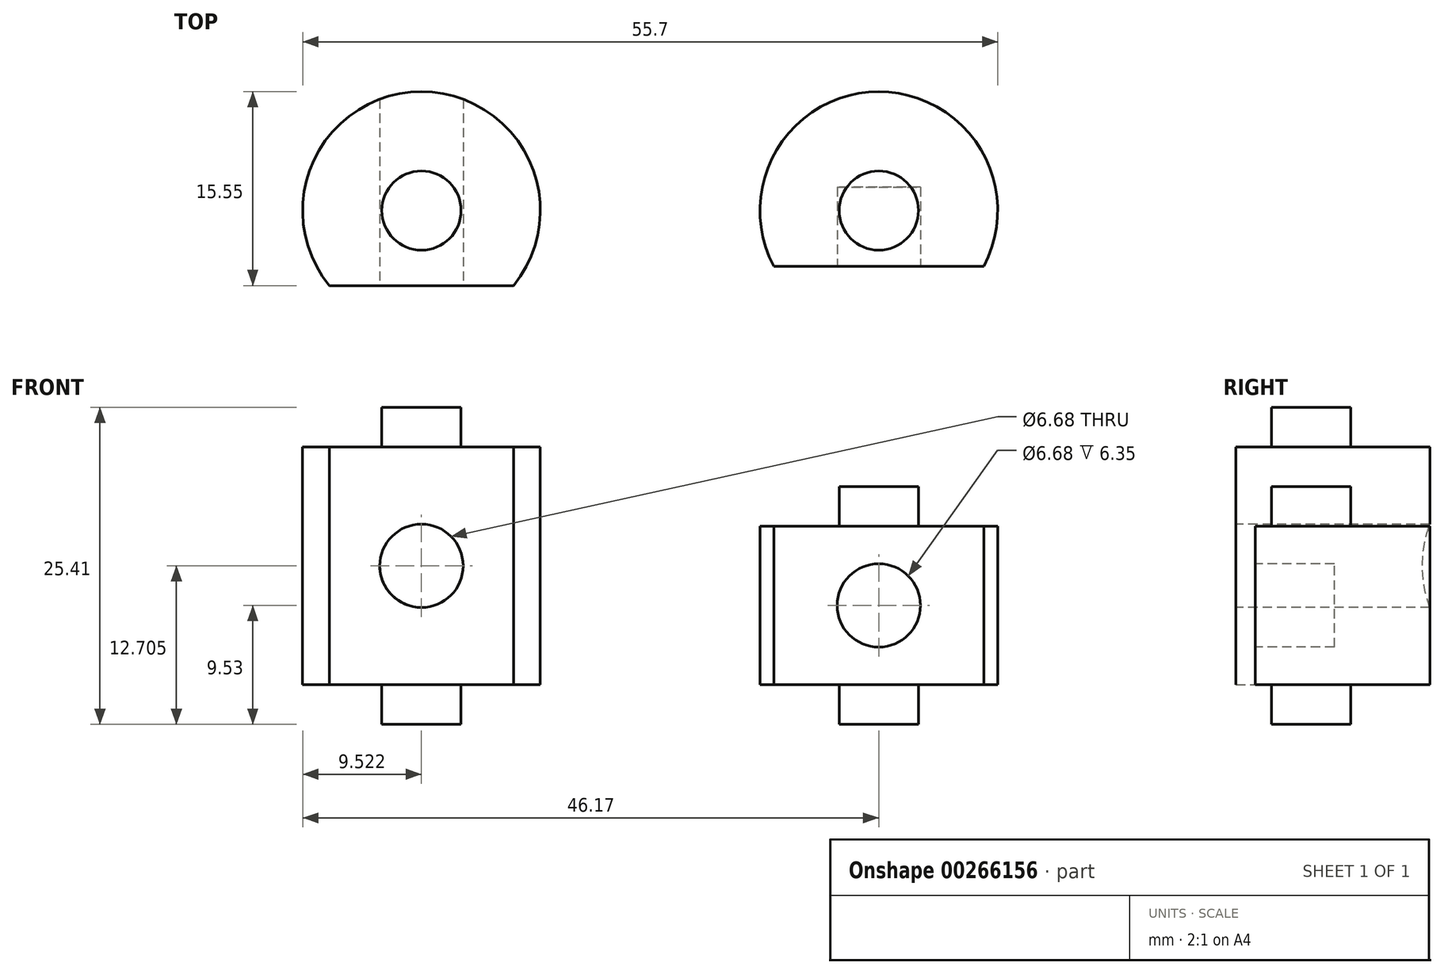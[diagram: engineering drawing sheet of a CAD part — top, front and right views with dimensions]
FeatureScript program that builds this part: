
annotation { "Feature Type Name" : "Feature", "Feature Type Description" : "" }
export const myFeature = defineFeature(function(context is Context, id is Id, definition is map)
    precondition{}
    {
        {
            var Q0;
            Q0=qCreatedBy(makeId("Top.planeOp"),FACE);
            var sketch = newSketch(context, id + "F0", { "sketchPlane" : qUnion([Q0])});
            skCircle(sketch, "E0", {"center": v(0, 0) * mm, "radius": 9.53 * mm});
            skSolve(sketch);
        }
        {
            var Q0;
            Q0=makeQuery(id+"F0.imprint","IMPRINT",FACE,{"disambiguationData":[TD([[makeQuery(id+"F0.imprint","IMPRINT",EDGE,{"derivedFrom":sQuery(id+"F0.wireOp",EDGE,"E0")}),1.0]])]});
            extrude(context, id + "F1", {"entities" : qUnion([Q0]), "depth" : 12.7 * mm});
        }
        {
            var Q0;
            Q0=makeQuery(id+"F1.opExtrude","CAP_FACE",FACE,{"disambiguationData":[OSD([sQuery(id+"F0.wireOp",EDGE,"E0")])],"isStart":false});
            var sketch = newSketch(context, id + "F2", { "sketchPlane" : qUnion([Q0])});
            skCircle(sketch, "E1", {"center": v(0, 0) * mm, "radius": 3.18 * mm});
            skSolve(sketch);
        }
        {
            var Q0;
            Q0=makeQuery(id+"F2.imprint","IMPRINT",FACE,{"disambiguationData":[TD([[makeQuery(id+"F2.imprint","IMPRINT",EDGE,{"derivedFrom":sQuery(id+"F2.wireOp",EDGE,"E1")}),1.0]])]});
            extrude(context, id + "F3", {"entities" : qUnion([Q0]), "operationType" : NewBodyOperationType.ADD, "depth" : 3.17 * mm});
        }
        {
            var Q0;
            Q0=makeQuery(id+"F1.opExtrude","CAP_FACE",FACE,{"disambiguationData":[OSD([sQuery(id+"F0.wireOp",EDGE,"E0")])],"isStart":true});
            var sketch = newSketch(context, id + "F4", { "sketchPlane" : qUnion([Q0])});
            skCircle(sketch, "E2", {"center": v(0, 0) * mm, "radius": 3.18 * mm});
            skSolve(sketch);
        }
        {
            var Q0;
            Q0=makeQuery(id+"F4.imprint","IMPRINT",FACE,{"disambiguationData":[TD([[makeQuery(id+"F4.imprint","IMPRINT",EDGE,{"derivedFrom":sQuery(id+"F4.wireOp",EDGE,"E2")}),1.0]])]});
            extrude(context, id + "F5", {"entities" : qUnion([Q0]), "operationType" : NewBodyOperationType.ADD, "depth" : 3.17 * mm});
        }
        {
            var Q0;
            Q0=qCreatedBy(makeId("Top.planeOp"),FACE);
            var sketch = newSketch(context, id + "F6", { "sketchPlane" : qUnion([Q0])});
            skCircle(sketch, "E3", {"center": v(-36.65, 0) * mm, "radius": 9.53 * mm});
            skSolve(sketch);
        }
        {
            var Q0;
            Q0=makeQuery(id+"F6.imprint","IMPRINT",FACE,{"disambiguationData":[TD([[makeQuery(id+"F6.imprint","IMPRINT",EDGE,{"derivedFrom":sQuery(id+"F6.wireOp",EDGE,"E3")}),1.0]])]});
            extrude(context, id + "F7", {"entities" : qUnion([Q0]), "depth" : 19.05 * mm});
        }
        {
            var Q0;
            Q0=makeQuery(id+"F7.opExtrude","CAP_FACE",FACE,{"disambiguationData":[OSD([sQuery(id+"F6.wireOp",EDGE,"E3")])],"isStart":false});
            var sketch = newSketch(context, id + "F8", { "sketchPlane" : qUnion([Q0])});
            skCircle(sketch, "E4", {"center": v(-36.65, 0) * mm, "radius": 3.18 * mm});
            skSolve(sketch);
        }
        {
            var Q0;
            Q0=makeQuery(id+"F7.opExtrude","CAP_FACE",FACE,{"disambiguationData":[OSD([sQuery(id+"F6.wireOp",EDGE,"E3")])],"isStart":true});
            var sketch = newSketch(context, id + "F9", { "sketchPlane" : qUnion([Q0])});
            skCircle(sketch, "E5", {"center": v(-36.65, 0) * mm, "radius": 3.18 * mm});
            skSolve(sketch);
        }
        {
            var Q0;
            Q0=makeQuery(id+"F9.imprint","IMPRINT",FACE,{"disambiguationData":[TD([[makeQuery(id+"F9.imprint","IMPRINT",EDGE,{"derivedFrom":sQuery(id+"F9.wireOp",EDGE,"E5")}),1.0]])]});
            extrude(context, id + "F10", {"entities" : qUnion([Q0]), "operationType" : NewBodyOperationType.ADD, "depth" : 3.17 * mm});
        }
        {
            var Q0;
            Q0=makeQuery(id+"F8.imprint","IMPRINT",FACE,{"disambiguationData":[TD([[makeQuery(id+"F8.imprint","IMPRINT",EDGE,{"derivedFrom":sQuery(id+"F8.wireOp",EDGE,"E4")}),1.0]])]});
            extrude(context, id + "F11", {"entities" : qUnion([Q0]), "operationType" : NewBodyOperationType.ADD, "depth" : 3.17 * mm});
        }
        {
            var Q0;
            Q0=makeQuery(id+"F1.opExtrude","CAP_FACE",FACE,{"disambiguationData":[OSD([sQuery(id+"F0.wireOp",EDGE,"E0")])],"isStart":false});
            var sketch = newSketch(context, id + "F12", { "sketchPlane" : qUnion([Q0])});
            skLineSegment(sketch, "E6", {"start": v(-8.4, -4.47) * mm, "end": v(8.4, -4.47) * mm});
            skSolve(sketch);
        }
        {
            var Q0;
            {var subQ0=sQuery(id+"F12.wireOp",EDGE,"E6");Q0=makeQuery(id+"F12.imprint","IMPRINT",FACE,{"disambiguationData":[TD([[makeQuery(id+"F12.imprint","IMPRINT",EDGE,{"derivedFrom":subQ0}),-1.0]])]});}
            extrude(context, id + "F13", {"entities" : qUnion([Q0]), "operationType" : NewBodyOperationType.REMOVE, "oppositeDirection" : true, "depth" : 12.7 * mm});
        }
        {
            var Q0;
            Q0=makeQuery(id+"F13.boolean.opBoolean","COPY",FACE,{"derivedFrom":makeQuery(id+"F13.opExtrude","SWEPT_FACE",FACE,{"disambiguationData":[OSD([sQuery(id+"F12.wireOp",EDGE,"E6")])]})});
            var sketch = newSketch(context, id + "F14", { "sketchPlane" : qUnion([Q0])});
            skCircle(sketch, "E7", {"center": v(0, 6.35) * mm, "radius": 3.34 * mm});
            skSolve(sketch);
        }
        {
            var Q0;
            Q0=makeQuery(id+"F14.imprint","IMPRINT",FACE,{"disambiguationData":[TD([[makeQuery(id+"F14.imprint","IMPRINT",EDGE,{"derivedFrom":sQuery(id+"F14.wireOp",EDGE,"E7")}),1.0]])]});
            extrude(context, id + "F15", {"entities" : qUnion([Q0]), "operationType" : NewBodyOperationType.REMOVE, "oppositeDirection" : true, "depth" : 6.35 * mm});
        }
        {
            var Q0;
            Q0=makeQuery(id+"F7.opExtrude","CAP_FACE",FACE,{"disambiguationData":[OSD([sQuery(id+"F6.wireOp",EDGE,"E3")])],"isStart":false});
            var sketch = newSketch(context, id + "F16", { "sketchPlane" : qUnion([Q0])});
            skLineSegment(sketch, "E8", {"start": v(-44.03, -6.02) * mm, "end": v(-29.26, -6.02) * mm});
            skSolve(sketch);
        }
        {
            var Q0;
            {var subQ0=sQuery(id+"F16.wireOp",EDGE,"E8");Q0=makeQuery(id+"F16.imprint","IMPRINT",FACE,{"disambiguationData":[TD([[makeQuery(id+"F16.imprint","IMPRINT",EDGE,{"derivedFrom":subQ0}),-1.0]])]});}
            extrude(context, id + "F17", {"entities" : qUnion([Q0]), "operationType" : NewBodyOperationType.REMOVE, "oppositeDirection" : true, "depth" : 19.05 * mm});
        }
        {
            var Q0;
            Q0=makeQuery(id+"F17.boolean.opBoolean","COPY",FACE,{"derivedFrom":makeQuery(id+"F17.opExtrude","SWEPT_FACE",FACE,{"disambiguationData":[OSD([sQuery(id+"F16.wireOp",EDGE,"E8")])]})});
            var sketch = newSketch(context, id + "F18", { "sketchPlane" : qUnion([Q0])});
            skCircle(sketch, "E9", {"center": v(-36.65, 9.52) * mm, "radius": 3.34 * mm});
            skSolve(sketch);
        }
        {
            var Q0;
            Q0=makeQuery(id+"F18.imprint","IMPRINT",FACE,{"disambiguationData":[TD([[makeQuery(id+"F18.imprint","IMPRINT",EDGE,{"derivedFrom":sQuery(id+"F18.wireOp",EDGE,"E9")}),1.0]])]});
            extrude(context, id + "F19", {"entities" : qUnion([Q0]), "operationType" : NewBodyOperationType.REMOVE, "oppositeDirection" : true, "depth" : 25.4 * mm});
        }
    });
